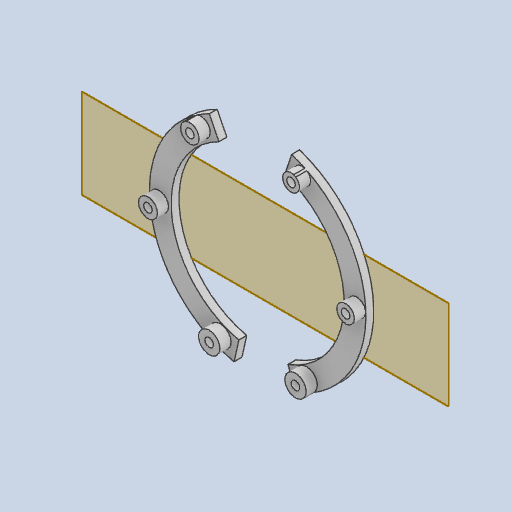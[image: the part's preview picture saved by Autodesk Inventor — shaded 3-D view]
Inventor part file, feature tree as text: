
AUTODESK INVENTOR PART (.ipt)
format: ipt  version: 2023.1 (Build 271208000, 208)  size: 560,128 bytes
history: native  units: in
note: dims shown in document units (in); Inventor stores cm internally (conversion verified against a paired STEP export)
features: other x6, reference x4, plane x2, extrude x2, sketch x2
ambient origin geometry x8: Origin, YZ Plane, XZ Plane, XY Plane, X Axis, Y Axis, Z Axis, Center Point
bodies: Solid1 (feature_tree)
feature tree (16):
  plane  "Work Plane1"
  extrude  "Extrusion1"  Depth=0.1181in TaperAngle=0.0deg
  plane  "Work Plane2"
  extrude  "Extrusion2"  [1 undecoded]
  sketch  "Sketch1"  dims[d0=0.2756in d1=0.0in d2=0.1181in d3=0.0in]
  reference  "Reference1"
  reference  "Reference2"
  sketch  "Sketch2"
  reference  "Reference3"
  reference  "Reference4"
  other  "G:\Assembly3.iam"
  other  "Assembly3.iam"
  other  "Part3:1"
  other  "G:\Assembly1.iam"
  other  "Assembly1.iam"
  other  "Part48:1"
note: 1 required parameter value undecoded (feature->parameter linkage not recoverable at this tier; creation-order binding heuristic only, values carry confidence <= 0.55)
